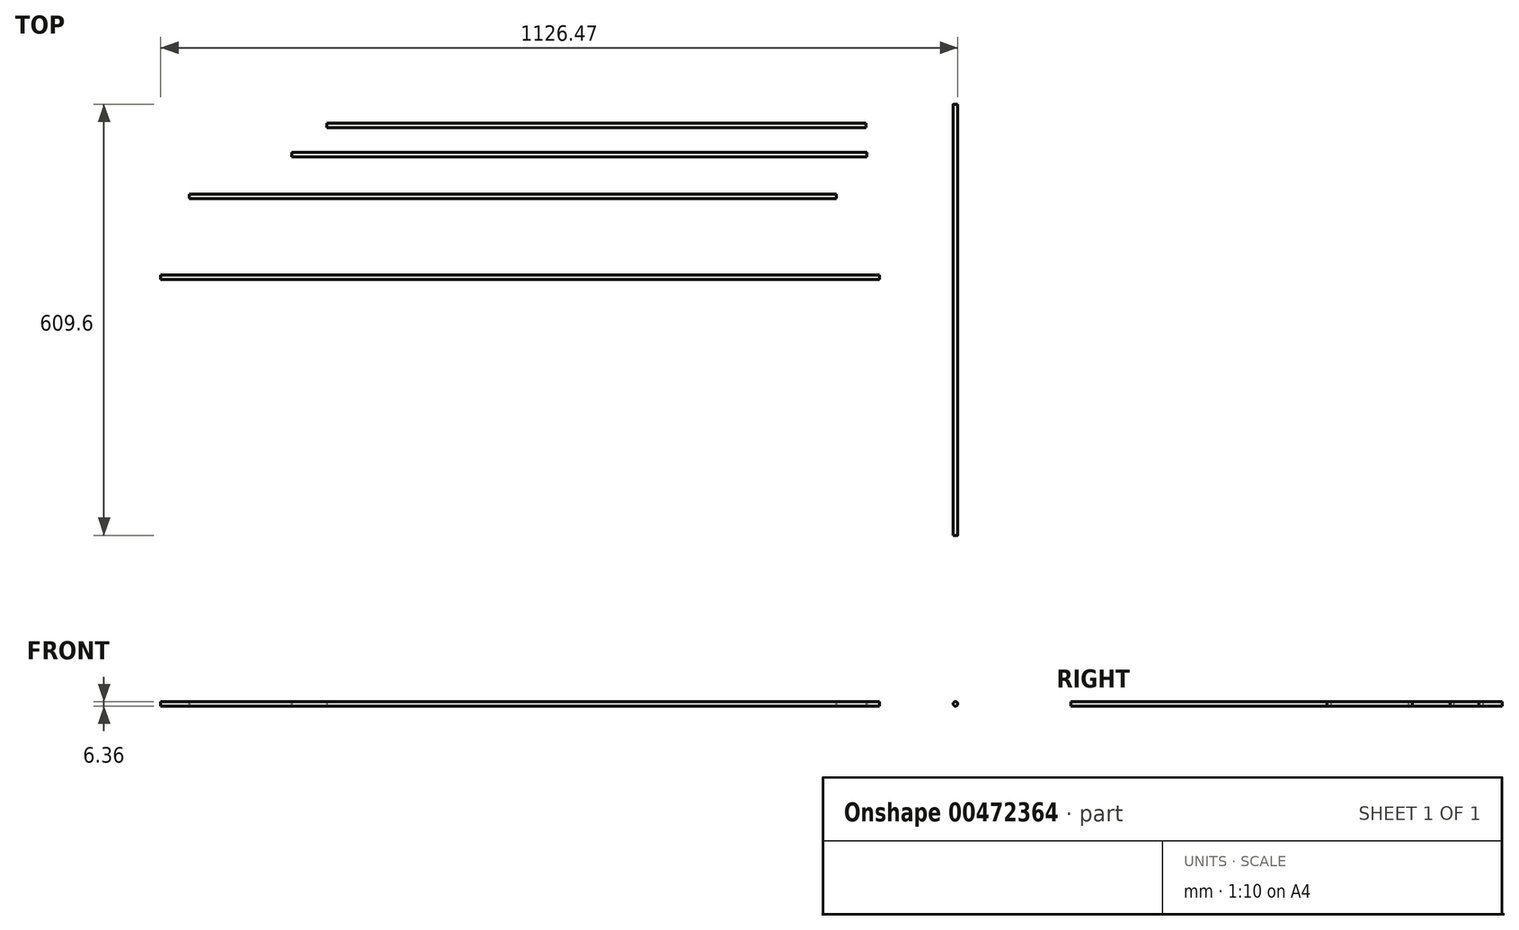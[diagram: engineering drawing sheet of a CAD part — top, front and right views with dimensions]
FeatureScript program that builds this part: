
annotation { "Feature Type Name" : "Feature", "Feature Type Description" : "" }
export const myFeature = defineFeature(function(context is Context, id is Id, definition is map)
    precondition{}
    {
        {
            var Q0;
            Q0=qCreatedBy(makeId("Top.planeOp"),FACE);
            var sketch = newSketch(context, id + "F0", { "sketchPlane" : qUnion([Q0])});
            skLineSegment(sketch, "E0.bottom", {"start": v(-491.41, -36.26) * mm, "end": v(524.59, -36.26) * mm});
            skLineSegment(sketch, "E0.top", {"start": v(-491.41, -33.08) * mm, "end": v(524.59, -33.08) * mm});
            skLineSegment(sketch, "E0.left", {"start": v(-491.41, -36.26) * mm, "end": v(-491.41, -33.08) * mm});
            skLineSegment(sketch, "E0.right", {"start": v(524.59, -36.26) * mm, "end": v(524.59, -33.08) * mm});
            skSolve(sketch);
        }
        {
            var Q0;
            Q0=makeQuery(id+"F0.imprint","IMPRINT",FACE,{"disambiguationData":[TD([[makeQuery(id+"F0.imprint","IMPRINT",EDGE,{"derivedFrom":sQuery(id+"F0.wireOp",EDGE,"E0.bottom")}),1.0]])]});
            var Q1;
            Q1=sQuery(id+"F0.wireOp",EDGE,"E0.bottom");
            revolve(context, id + "F1", {"entities" : qUnion([Q0]), "axis" : qUnion([Q1]), "revolveType" : RevolveType.FULL});
        }
        {
            var Q0;
            Q0=qCreatedBy(makeId("Top.planeOp"),FACE);
            var sketch = newSketch(context, id + "F2", { "sketchPlane" : qUnion([Q0])});
            skLineSegment(sketch, "E1.bottom", {"start": v(-450.94, 75.15) * mm, "end": v(463.46, 75.15) * mm});
            skLineSegment(sketch, "E1.top", {"start": v(-450.94, 78.32) * mm, "end": v(463.46, 78.32) * mm});
            skLineSegment(sketch, "E1.left", {"start": v(-450.94, 75.15) * mm, "end": v(-450.94, 78.32) * mm});
            skLineSegment(sketch, "E1.right", {"start": v(463.46, 75.15) * mm, "end": v(463.46, 78.32) * mm});
            skSolve(sketch);
        }
        {
            var Q0;
            Q0=qCreatedBy(makeId("Top.planeOp"),FACE);
            var sketch = newSketch(context, id + "F3", { "sketchPlane" : qUnion([Q0])});
            skLineSegment(sketch, "E2.bottom", {"start": v(-306.45, 134.2) * mm, "end": v(506.35, 134.2) * mm});
            skLineSegment(sketch, "E2.top", {"start": v(-306.45, 137.38) * mm, "end": v(506.35, 137.38) * mm});
            skLineSegment(sketch, "E2.left", {"start": v(-306.45, 134.2) * mm, "end": v(-306.45, 137.38) * mm});
            skLineSegment(sketch, "E2.right", {"start": v(506.35, 134.2) * mm, "end": v(506.35, 137.38) * mm});
            skSolve(sketch);
        }
        {
            var Q0;
            Q0=qCreatedBy(makeId("Top.planeOp"),FACE);
            var sketch = newSketch(context, id + "F4", { "sketchPlane" : qUnion([Q0])});
            skLineSegment(sketch, "E3.bottom", {"start": v(-256.94, 175.31) * mm, "end": v(505.06, 175.31) * mm});
            skLineSegment(sketch, "E3.top", {"start": v(-256.94, 178.49) * mm, "end": v(505.06, 178.49) * mm});
            skLineSegment(sketch, "E3.left", {"start": v(-256.94, 175.31) * mm, "end": v(-256.94, 178.49) * mm});
            skLineSegment(sketch, "E3.right", {"start": v(505.06, 175.31) * mm, "end": v(505.06, 178.49) * mm});
            skSolve(sketch);
        }
        {
            var Q0;
            Q0=makeQuery(id+"F2.imprint","IMPRINT",FACE,{"disambiguationData":[TD([[makeQuery(id+"F2.imprint","IMPRINT",EDGE,{"derivedFrom":sQuery(id+"F2.wireOp",EDGE,"E1.bottom")}),1.0]])]});
            var Q1;
            Q1=sQuery(id+"F2.wireOp",EDGE,"E1.top");
            revolve(context, id + "F5", {"entities" : qUnion([Q0]), "axis" : qUnion([Q1]), "revolveType" : RevolveType.FULL});
        }
        {
            var Q0;
            Q0=makeQuery(id+"F3.imprint","IMPRINT",FACE,{"disambiguationData":[TD([[makeQuery(id+"F3.imprint","IMPRINT",EDGE,{"derivedFrom":sQuery(id+"F3.wireOp",EDGE,"E2.bottom")}),1.0]])]});
            var Q1;
            Q1=sQuery(id+"F3.wireOp",EDGE,"E2.top");
            revolve(context, id + "F6", {"entities" : qUnion([Q0]), "axis" : qUnion([Q1]), "revolveType" : RevolveType.FULL});
        }
        {
            var Q0;
            Q0=makeQuery(id+"F4.imprint","IMPRINT",FACE,{"disambiguationData":[TD([[makeQuery(id+"F4.imprint","IMPRINT",EDGE,{"derivedFrom":sQuery(id+"F4.wireOp",EDGE,"E3.bottom")}),1.0]])]});
            var Q1;
            Q1=sQuery(id+"F4.wireOp",EDGE,"E3.top");
            revolve(context, id + "F7", {"entities" : qUnion([Q0]), "axis" : qUnion([Q1]), "revolveType" : RevolveType.FULL});
        }
        {
            var Q0;
            Q0=qCreatedBy(makeId("Top.planeOp"),FACE);
            var sketch = newSketch(context, id + "F8", { "sketchPlane" : qUnion([Q0])});
            skLineSegment(sketch, "E4.bottom", {"start": v(628.7, 208.3) * mm, "end": v(631.88, 208.3) * mm});
            skLineSegment(sketch, "E4.top", {"start": v(628.7, -401.3) * mm, "end": v(631.88, -401.3) * mm});
            skLineSegment(sketch, "E4.left", {"start": v(628.7, 208.3) * mm, "end": v(628.7, -401.3) * mm});
            skLineSegment(sketch, "E4.right", {"start": v(631.88, 208.3) * mm, "end": v(631.88, -401.3) * mm});
            skSolve(sketch);
        }
        {
            var Q0;
            Q0=qCreatedBy(makeId("Top.planeOp"),FACE);
            var sketch = newSketch(context, id + "F9", { "sketchPlane" : qUnion([Q0])});
            skLineSegment(sketch, "E5.bottom", {"start": v(710.22, 388.58) * mm, "end": v(713.4, 388.58) * mm});
            skLineSegment(sketch, "E5.top", {"start": v(710.22, -525.82) * mm, "end": v(713.4, -525.82) * mm});
            skLineSegment(sketch, "E5.left", {"start": v(710.22, 388.58) * mm, "end": v(710.22, -525.82) * mm});
            skLineSegment(sketch, "E5.right", {"start": v(713.4, 388.58) * mm, "end": v(713.4, -525.82) * mm});
            skSolve(sketch);
        }
        {
            var Q0;
            Q0=makeQuery(id+"F8.imprint","IMPRINT",FACE,{"disambiguationData":[TD([[makeQuery(id+"F8.imprint","IMPRINT",EDGE,{"derivedFrom":sQuery(id+"F8.wireOp",EDGE,"E4.bottom")}),-1.0]])]});
            var Q1;
            Q1=sQuery(id+"F8.wireOp",EDGE,"E4.right");
            revolve(context, id + "F10", {"entities" : qUnion([Q0]), "axis" : qUnion([Q1]), "revolveType" : RevolveType.FULL});
        }
        {
            var Q0;
            Q0=makeQuery(id+"F9.imprint","IMPRINT",FACE,{"disambiguationData":[TD([[makeQuery(id+"F9.imprint","IMPRINT",EDGE,{"derivedFrom":sQuery(id+"F9.wireOp",EDGE,"E5.bottom")}),-1.0]])]});
            var Q1;
            Q1=sQuery(id+"F9.wireOp",EDGE,"E5.right");
            revolve(context, id + "F11", {"entities" : qUnion([Q0]), "axis" : qUnion([Q1]), "revolveType" : RevolveType.FULL});
        }
        {
            var Q0;
            Q0=makeQuery(id+"F11.opRevolve","SWEPT_BODY",BODY,{"disambiguationData":[OSD([sQuery(id+"F9.wireOp",EDGE,"E5.bottom"),sQuery(id+"F9.wireOp",EDGE,"E5.top"),sQuery(id+"F9.wireOp",EDGE,"E5.left"),sQuery(id+"F9.wireOp",EDGE,"E5.right")])]});
            deleteBodies(context, id + "F12", {"entities" : qUnion([Q0])});
        }
    });
